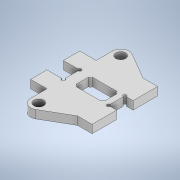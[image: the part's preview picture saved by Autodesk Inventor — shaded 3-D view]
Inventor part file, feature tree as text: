
AUTODESK INVENTOR PART (.ipt)
format: ipt  version: 2021 (Build 250183000, 183)  size: 161,280 bytes
history: native  units: mm
features: extrude x1, sketch x1
ambient origin geometry x8: Origin, YZ Plane, XZ Plane, XY Plane, X Axis, Y Axis, Z Axis, Center Point
bodies: Solid1 (feature_tree)
feature tree (2):
  extrude  "Extrusion1"  Depth=40.0mm
  sketch  "Sketch1"  dims[d4=10.0mm d5=40.0mm d6=50.0mm d7=20.0mm d8=65.0mm d9=85.0mm d10=30.0mm d11=10.0mm d12=30.0deg d13=12.0mm d14=20.0mm d15=85.0mm d17=20.0mm d18=65.0mm d19=10.0mm d20=13.0mm d21=35.0mm d22=4.0mm d23=5.0mm d24=5.0mm d25=4.0mm d26=10.0mm d27=0.0mm]
